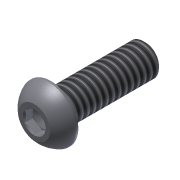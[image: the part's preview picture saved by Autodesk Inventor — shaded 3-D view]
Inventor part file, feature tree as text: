
AUTODESK INVENTOR PART (.ipt)
format: ipt  version: 2013 (Build 170138000, 138)  size: 204,288 bytes
history: native  units: in
note: dims shown in document units (in); Inventor stores cm internally (conversion verified against a paired STEP export)
features: extrude x2, sketch x2, other x1, imported_body x1, thread x1, chamfer x1
ambient origin geometry x8: Origin, YZ Plane, XZ Plane, XY Plane, X Axis, Y Axis, Z Axis, Center Point
feature tree (8):
  parser-record x1  (decoder bookkeeping rows leaked as tree rows — omitted from the tree; the rows remain in map.json)
  imported_body  "Base1"
  extrude  "Extrusion1"  Depth=1.0in TaperAngle=0.0deg
  extrude  "Extrusion2"  Depth=0.755in TaperAngle=0.0deg
  thread  "Thread1"  [1 undecoded]
  chamfer  "Chamfer1"  Distance=0.02in Angle=45.0deg
  sketch  "Sketch1"  dims[d1=0.26in d2=1.0in d3=0.0in]
  sketch  "Sketch2"  dims[d4=0.25in d5=0.755in d6=0.0in d7=1.0in d8=0.0in d9=0.02in d10=0.125in d11=45.0deg]
note: 1 required parameter value undecoded (feature->parameter linkage not recoverable at this tier; creation-order binding heuristic only, values carry confidence <= 0.55)
